# Revit family: Quadro Combo WH Pan Soft Close Seat
name_source: partatom
category: Furniture
units: mm (PartAtom-declared; Revit-internal decimal feet)

## family parameters
Always vertical = No
Cut with Voids When Loaded = No
Enable Cutting in Views = Yes
Render Appearance Source = Family Geometry
Room Calculation Point = No
Shared = Yes

## types (1)
- Quadro Combo WH Pan Soft Close Seat
    Category = Wall Hung Pans
    Ceramic = Ceramic
    Colour = White
    Default Elevation = 0 mm  [stored 0 ft]
    Height = 0 mm  [stored 0 ft]
    Manufacturer = Lecico SA
    Material = Vitreous China
    Model = Quadro Combo WH Pan Soft Close Seat
    Product Code = QUADUOWHU0SCSBC
    Technical Dimensions = W363 x H364 x D486mm
    URL = https://www.lecicosa.co.za

note: [stored X ft] marks values corroborated as IEEE doubles in the binary element streams (Revit-internal decimal feet)

## geometry (parser evidence)
native form markers: Blend x2, Sweep x5
no freeform markers — native parametric forms only
